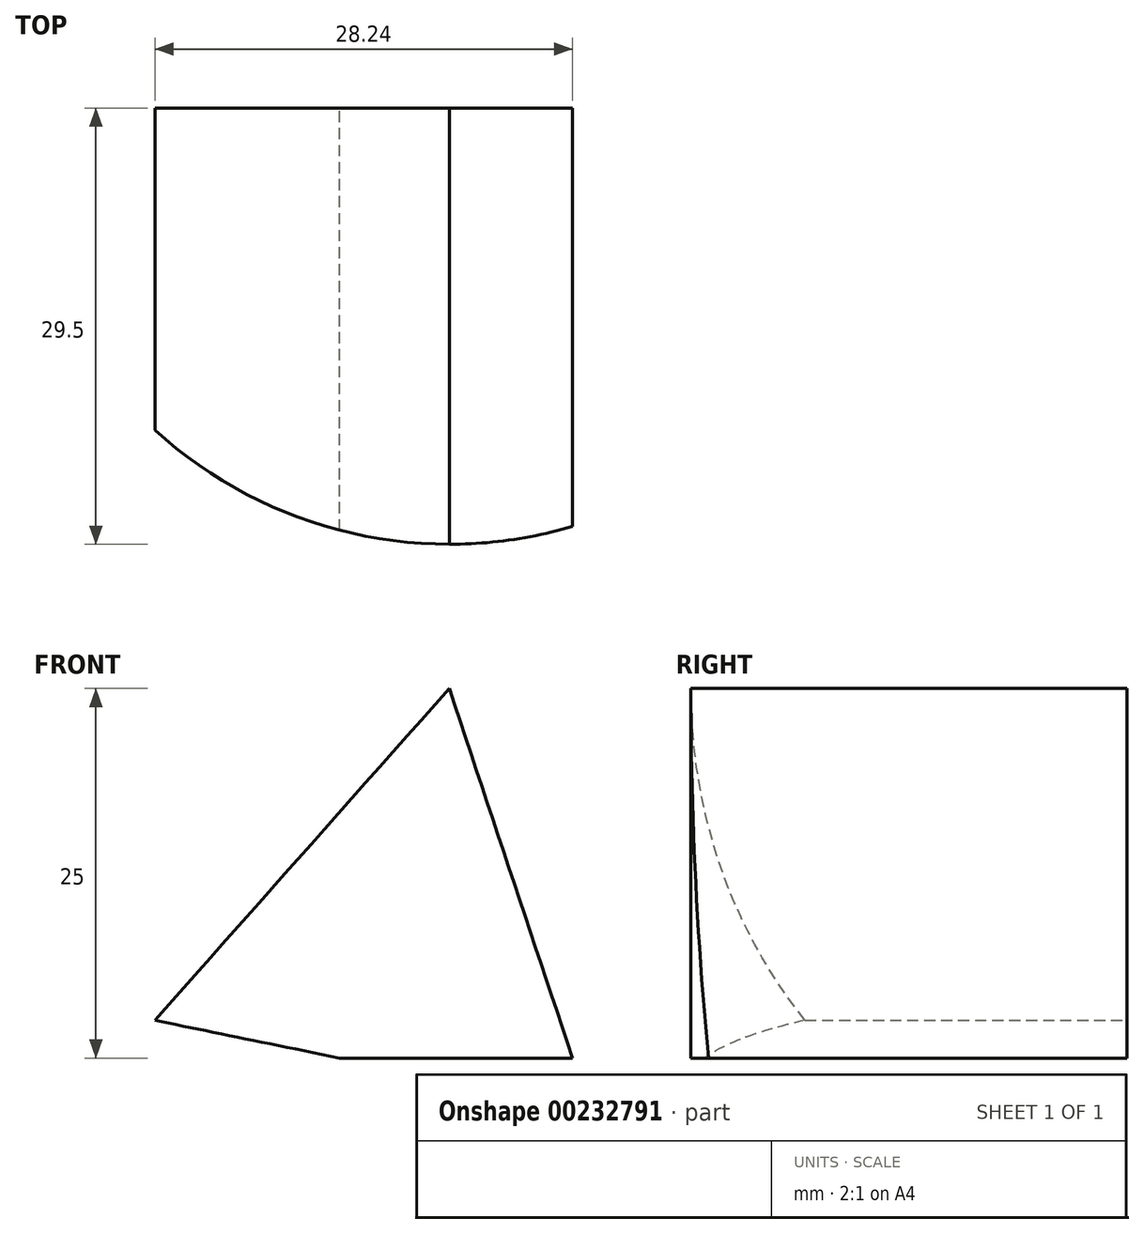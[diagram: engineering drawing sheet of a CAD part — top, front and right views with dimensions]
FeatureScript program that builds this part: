
annotation { "Feature Type Name" : "Feature", "Feature Type Description" : "" }
export const myFeature = defineFeature(function(context is Context, id is Id, definition is map)
    precondition{}
    {
        {
            var Q0;
            Q0=qCreatedBy(makeId("Top.planeOp"),FACE);
            var sketch = newSketch(context, id + "F0", { "sketchPlane" : qUnion([Q0])});
            skCircle(sketch, "E0", {"center": v(0, 0) * mm, "radius": 29.5 * mm});
            skSolve(sketch);
        }
        {
            var Q0;
            Q0=makeQuery(id+"F0.imprint","IMPRINT",FACE,{"disambiguationData":[TD([[makeQuery(id+"F0.imprint","IMPRINT",EDGE,{"derivedFrom":sQuery(id+"F0.wireOp",EDGE,"E0")}),1.0]])]});
            extrude(context, id + "F1", {"entities" : qUnion([Q0]), "oppositeDirection" : true, "depth" : 25 * mm});
        }
        {
            var Q0;
            Q0=qCreatedBy(makeId("Front.planeOp"),FACE);
            var sketch = newSketch(context, id + "F2", { "sketchPlane" : qUnion([Q0])});
            skLineSegment(sketch, "E1", {"start": v(-19.9, -22.45) * mm, "end": v(0, 0) * mm});
            skLineSegment(sketch, "E2", {"start": v(0, 0) * mm, "end": v(9.5, -28.46) * mm});
            skLineSegment(sketch, "E3", {"start": v(-19.9, -22.45) * mm, "end": v(9.5, -28.46) * mm});
            skSolve(sketch);
        }
        {
            var Q0;
            Q0=makeQuery(id+"F2.imprint","IMPRINT",FACE,{"disambiguationData":[TD([[makeQuery(id+"F2.imprint","IMPRINT",EDGE,{"derivedFrom":sQuery(id+"F2.wireOp",EDGE,"E1")}),-1.0]])]});
            extrude(context, id + "F3", {"entities" : qUnion([Q0]), "operationType" : NewBodyOperationType.INTERSECT, "depth" : 42.8 * mm});
        }
    });
